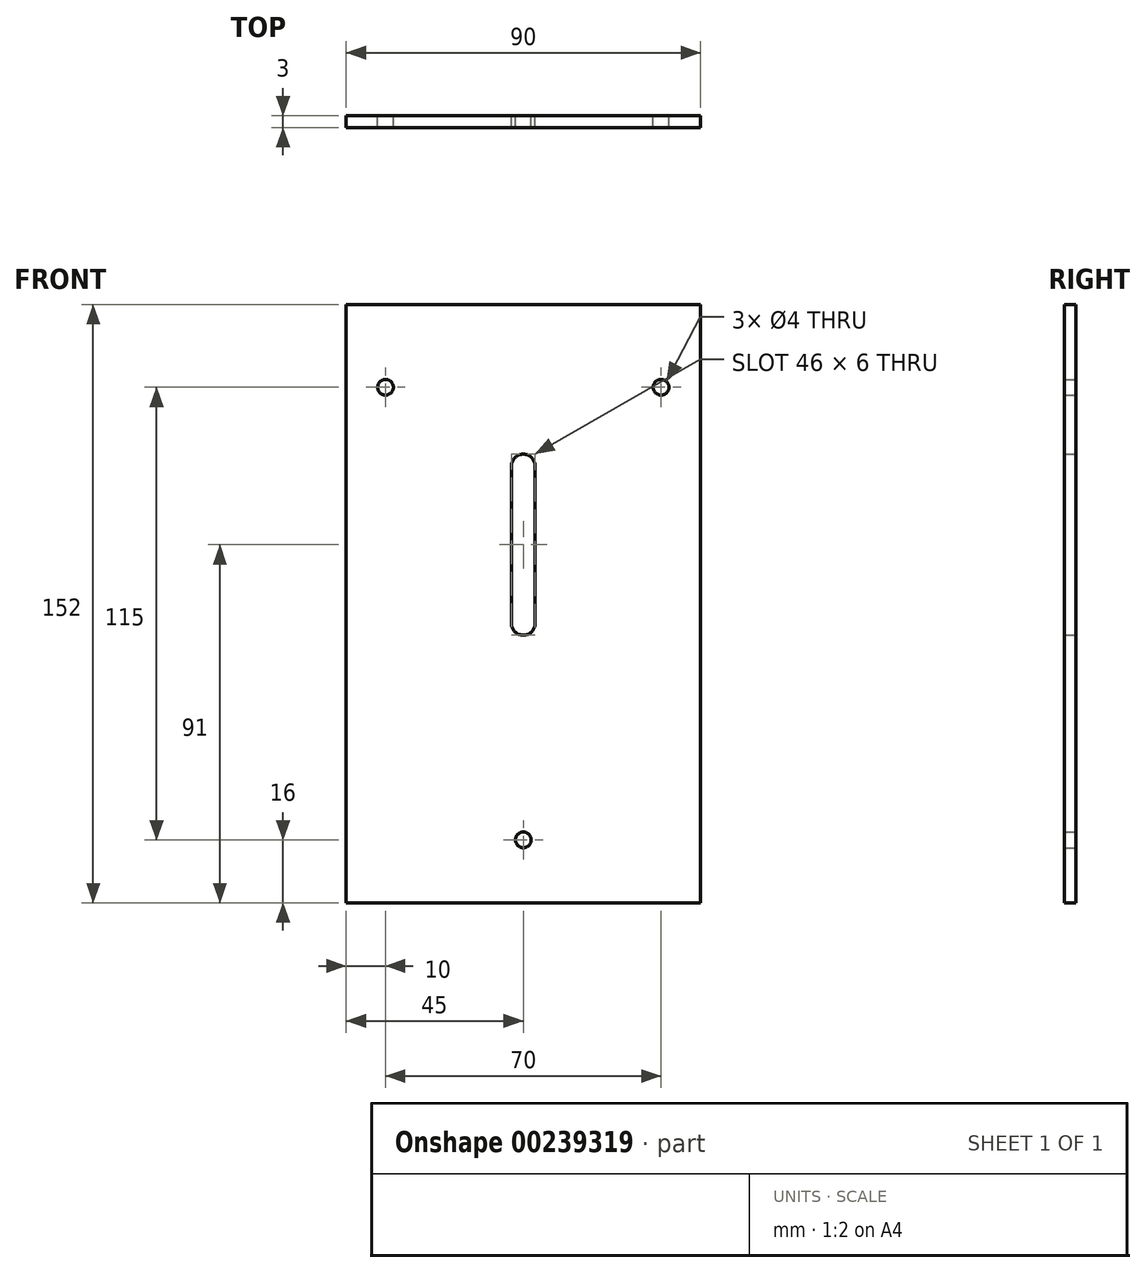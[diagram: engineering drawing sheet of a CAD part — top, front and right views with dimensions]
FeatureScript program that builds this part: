
annotation { "Feature Type Name" : "Feature", "Feature Type Description" : "" }
export const myFeature = defineFeature(function(context is Context, id is Id, definition is map)
    precondition{}
    {
        {
            var Q0;
            Q0=qCreatedBy(makeId("Front.planeOp"),FACE);
            var sketch = newSketch(context, id + "F0", { "sketchPlane" : qUnion([Q0])});
            skLineSegment(sketch, "E0.bottom", {"start": v(45, -76) * mm, "end": v(-45, -76) * mm});
            skLineSegment(sketch, "E0.top", {"start": v(45, 76) * mm, "end": v(-45, 76) * mm});
            skLineSegment(sketch, "E0.left", {"start": v(45, -76) * mm, "end": v(45, 76) * mm});
            skLineSegment(sketch, "E0.right", {"start": v(-45, -76) * mm, "end": v(-45, 76) * mm});
            skPoint(sketch, "E0.middle", {"position": v(0, 0) * mm});
            skCircle(sketch, "E1", {"center": v(0, -60) * mm, "radius": 2 * mm});
            skLineSegment(sketch, "E2.bottom", {"start": v(-3, -5) * mm, "end": v(3, -5) * mm, "construction": true});
            skLineSegment(sketch, "E2.top", {"start": v(-3, 35) * mm, "end": v(3, 35) * mm, "construction": true});
            skLineSegment(sketch, "E2.left", {"start": v(-3, -5) * mm, "end": v(-3, 35) * mm});
            skLineSegment(sketch, "E2.right", {"start": v(3, -5) * mm, "end": v(3, 35) * mm});
            skPoint(sketch, "E2.middle", {"position": v(0, 15) * mm});
            skArc(sketch, "E3", {"start": v(-3, -5) * mm, "mid": v(0, -8) * mm, "end": v(3, -5) * mm});
            skArc(sketch, "E4", {"start": v(3, 35) * mm, "mid": v(0, 38) * mm, "end": v(-3, 35) * mm});
            skCircle(sketch, "E5", {"center": v(35, 55) * mm, "radius": 2 * mm});
            skCircle(sketch, "E6", {"center": v(-35, 55) * mm, "radius": 2 * mm});
            skSolve(sketch);
        }
        {
            var Q0;
            Q0 = qSketchRegion(id + "F0", true);
            extrude(context, id + "F1", {"entities" : qUnion([Q0]), "depth" : 3 * mm});
        }
    });
